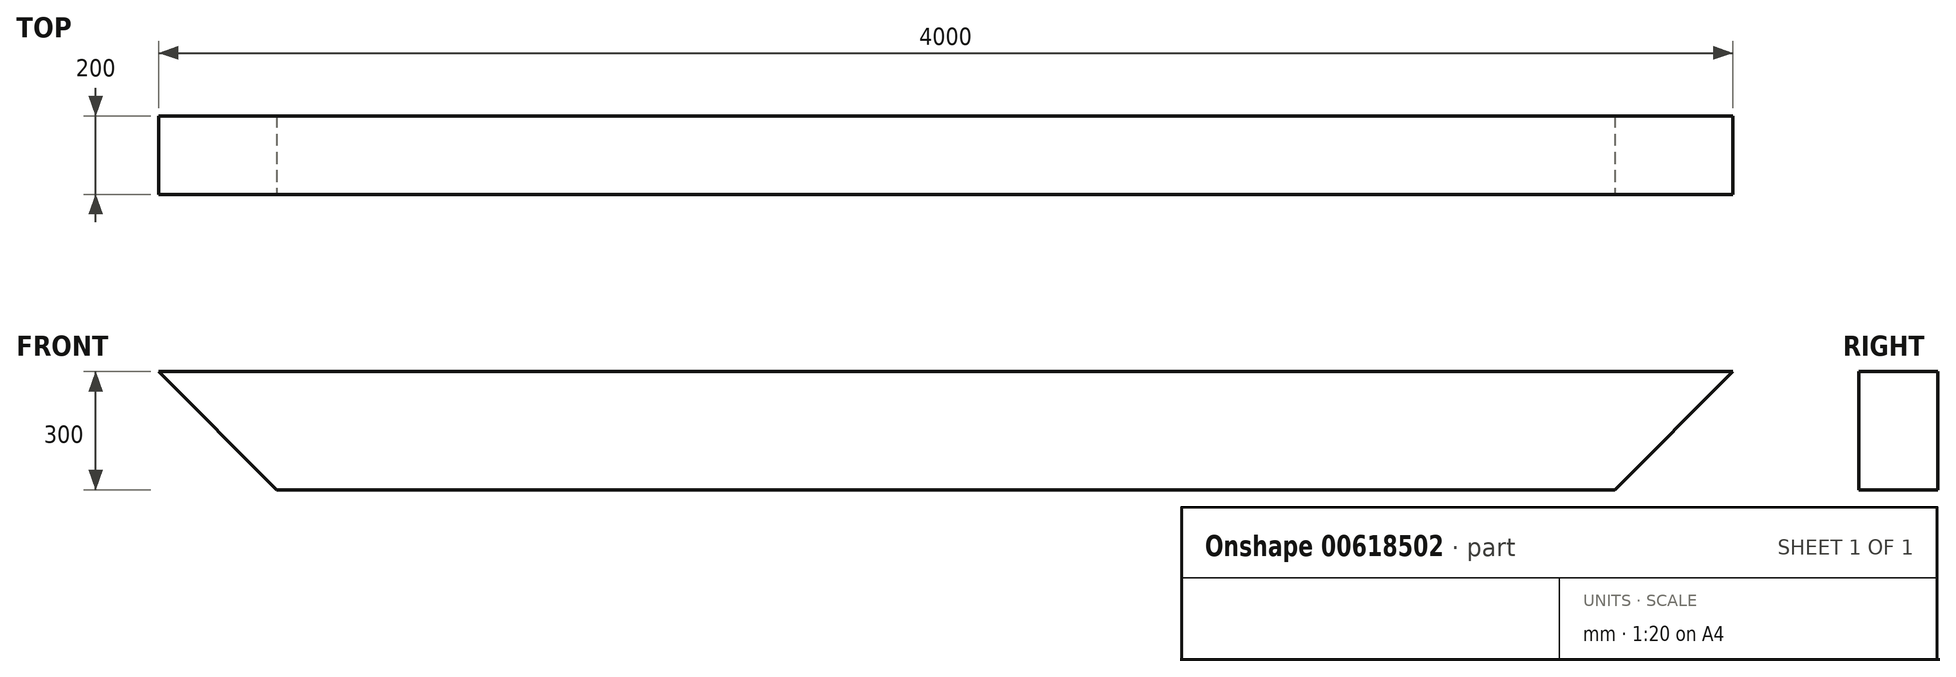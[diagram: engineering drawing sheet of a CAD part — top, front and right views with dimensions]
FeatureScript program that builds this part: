
annotation { "Feature Type Name" : "Feature", "Feature Type Description" : "" }
export const myFeature = defineFeature(function(context is Context, id is Id, definition is map)
    precondition{}
    {
        {
            var Q0;
            Q0=qCreatedBy(makeId("Front.planeOp"),FACE);
            var sketch = newSketch(context, id + "F0", { "sketchPlane" : qUnion([Q0])});
            skLineSegment(sketch, "E0", {"start": v(-2000, 300) * mm, "end": v(-1700, 0) * mm});
            skLineSegment(sketch, "E1", {"start": v(-1700, 0) * mm, "end": v(0, 0) * mm});
            skLineSegment(sketch, "E2", {"start": v(0, 0) * mm, "end": v(0, 734) * mm, "construction": true});
            skLineSegment(sketch, "E3.MirrorCS", {"start": v(2000, 300) * mm, "end": v(1700, 0) * mm});
            skLineSegment(sketch, "E4", {"start": v(-2000, 300) * mm, "end": v(2000, 300) * mm});
            skLineSegment(sketch, "E5", {"start": v(1700, 0) * mm, "end": v(0, 0) * mm});
            skSolve(sketch);
        }
        {
            var Q0;
            Q0 = qSketchRegion(id + "F0", true);
            extrude(context, id + "F1", {"entities" : qUnion([Q0]), "oppositeDirection" : true, "depth" : 200 * mm, "offsetDistance" : 25 * mm});
        }
    });
